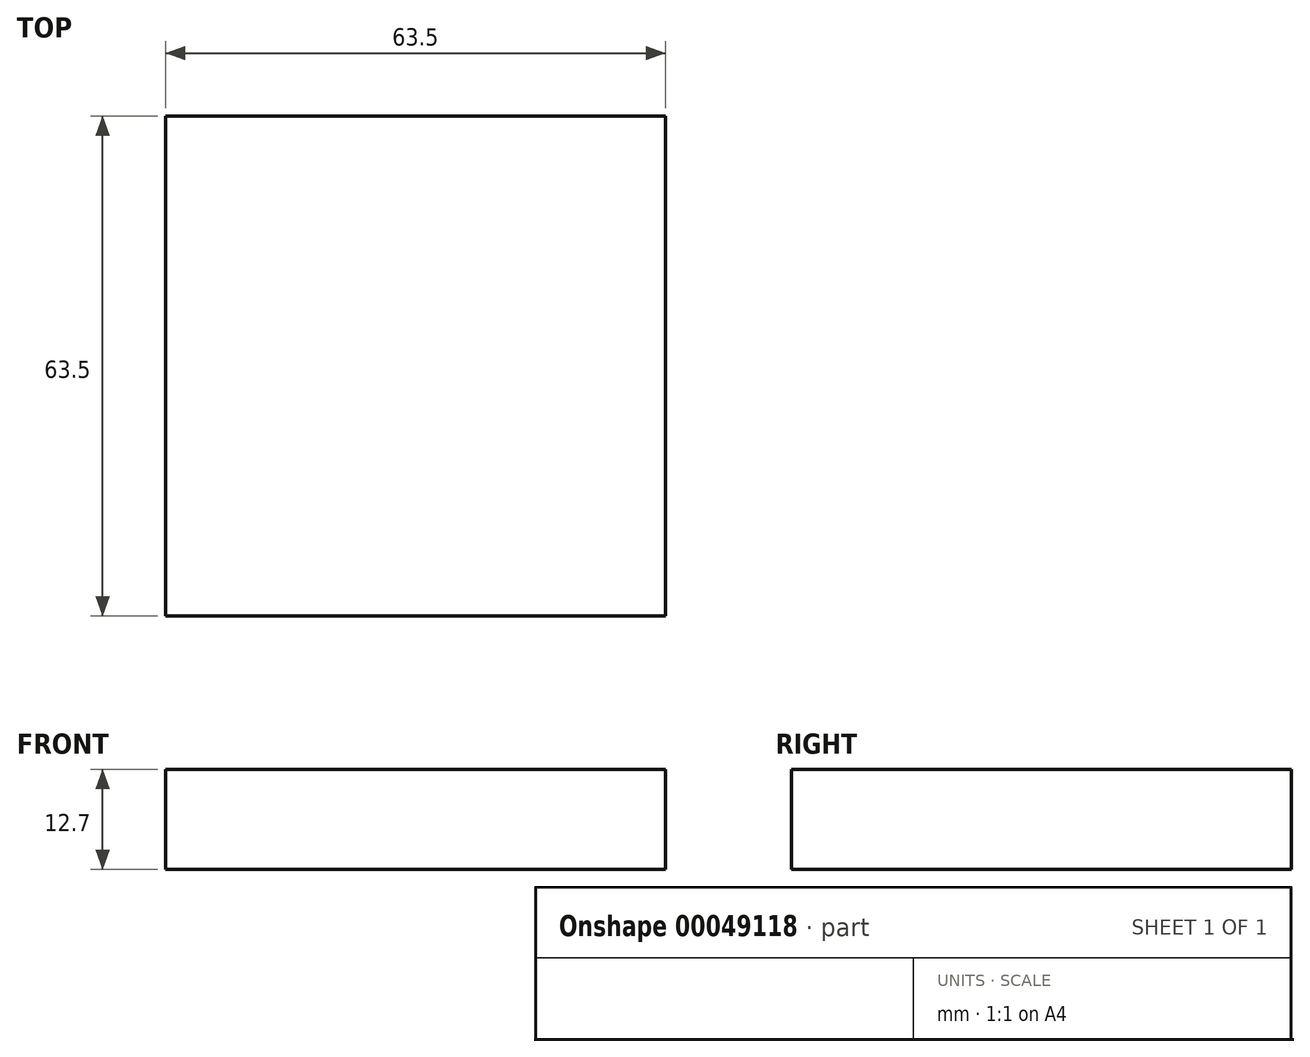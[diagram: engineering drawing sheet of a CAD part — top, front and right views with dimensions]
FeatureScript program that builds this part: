
annotation { "Feature Type Name" : "Feature", "Feature Type Description" : "" }
export const myFeature = defineFeature(function(context is Context, id is Id, definition is map)
    precondition{}
    {
        {
            var Q0;
            Q0=qCreatedBy(makeId("Top.planeOp"),FACE);
            var sketch = newSketch(context, id + "F0", { "sketchPlane" : qUnion([Q0])});
            skLineSegment(sketch, "E0.bottom", {"start": v(0, 0) * mm, "end": v(63.5, 0) * mm});
            skLineSegment(sketch, "E0.top", {"start": v(0, 63.5) * mm, "end": v(63.5, 63.5) * mm});
            skLineSegment(sketch, "E0.left", {"start": v(0, 0) * mm, "end": v(0, 63.5) * mm});
            skLineSegment(sketch, "E0.right", {"start": v(63.5, 0) * mm, "end": v(63.5, 63.5) * mm});
            skSolve(sketch);
        }
        {
            var Q0;
            Q0=sQuery(id+"F0.wireOp",EDGE,"E0.top");
            var Q1;
            Q1=sQuery(id+"F0.wireOp",EDGE,"E0.left");
            var Q2;
            Q2=sQuery(id+"F0.wireOp",EDGE,"E0.bottom");
            var Q3;
            Q3=sQuery(id+"F0.wireOp",EDGE,"E0.right");
            extrude(context, id + "F1", {"bodyType" : ToolBodyType.SURFACE, "surfaceEntities" : qUnion([Q0, Q1, Q2, Q3]), "depth" : 12.7 * mm});
        }
    });
